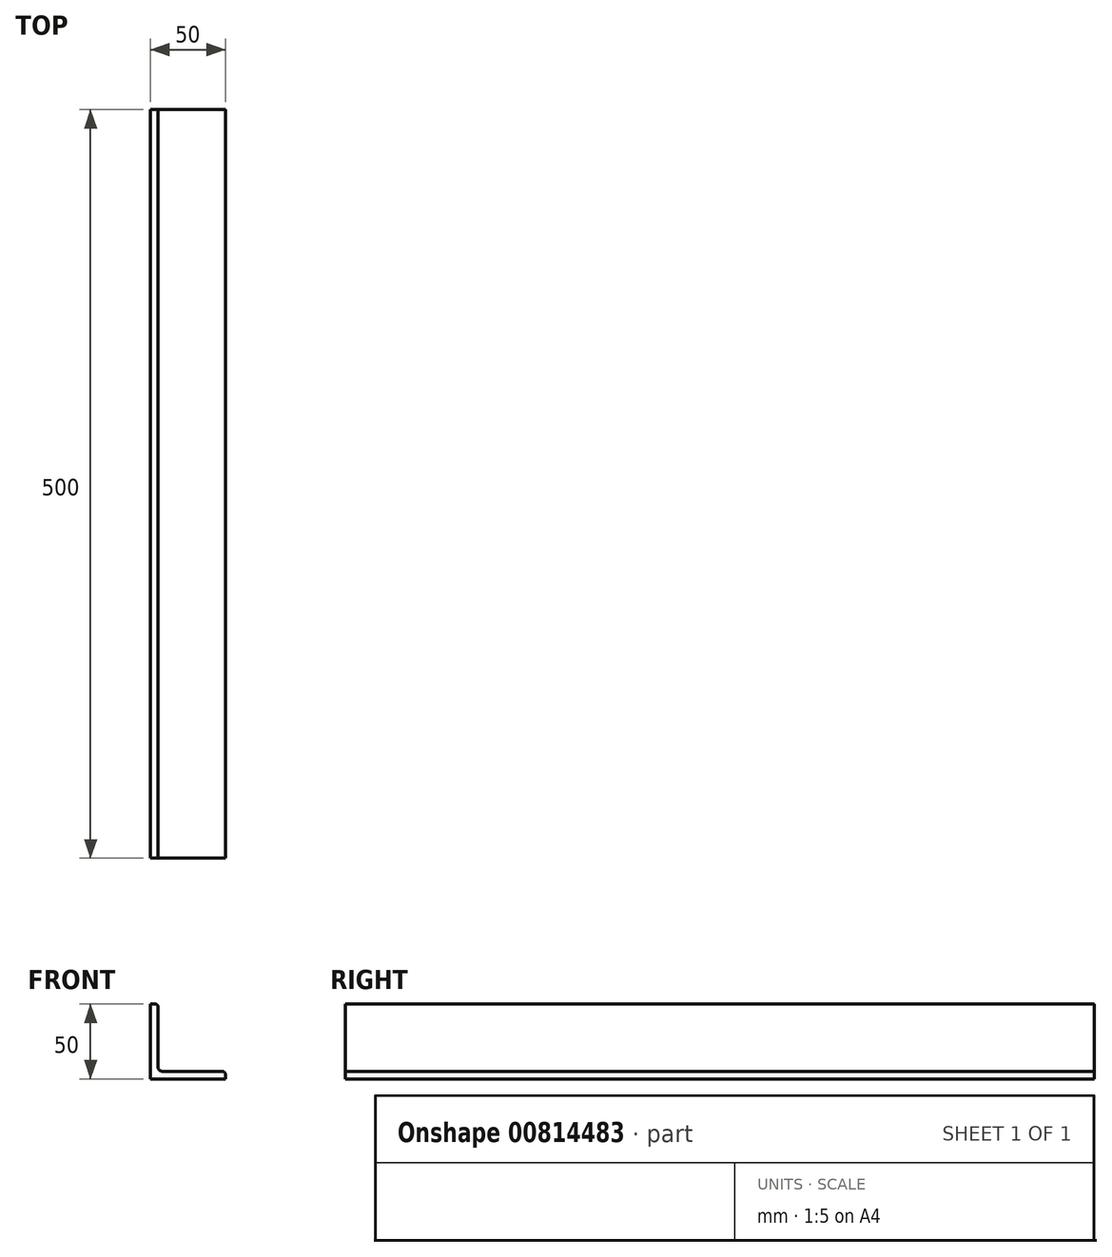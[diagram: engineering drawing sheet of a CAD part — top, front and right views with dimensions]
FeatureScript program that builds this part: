
annotation { "Feature Type Name" : "Feature", "Feature Type Description" : "" }
export const myFeature = defineFeature(function(context is Context, id is Id, definition is map)
    precondition{}
    {
        {
            var Q0;
            Q0=qCreatedBy(makeId("Front.planeOp"),FACE);
            var sketch = newSketch(context, id + "F0", { "sketchPlane" : qUnion([Q0])});
            skLineSegment(sketch, "E0", {"start": v(0, 0) * mm, "end": v(50, 0) * mm});
            skLineSegment(sketch, "E1", {"start": v(50, 0) * mm, "end": v(50, 3) * mm});
            skLineSegment(sketch, "E2", {"start": v(48, 5) * mm, "end": v(8, 5) * mm});
            skLineSegment(sketch, "E3", {"start": v(5, 8) * mm, "end": v(5, 48) * mm});
            skLineSegment(sketch, "E4", {"start": v(3, 50) * mm, "end": v(0, 50) * mm});
            skLineSegment(sketch, "E5", {"start": v(0, 50) * mm, "end": v(0, 0) * mm});
            skPoint(sketch, "E6.visualSharp", {"position": v(5, 50) * mm});
            skArc(sketch, "E6.filletArc", {"start": v(5, 48) * mm, "mid": v(4.41, 49.41) * mm, "end": v(3, 50) * mm});
            skPoint(sketch, "E7.visualSharp", {"position": v(50, 5) * mm});
            skArc(sketch, "E7.filletArc", {"start": v(50, 3) * mm, "mid": v(49.41, 4.41) * mm, "end": v(48, 5) * mm});
            skPoint(sketch, "E8.visualSharp", {"position": v(5, 5) * mm});
            skArc(sketch, "E8.filletArc", {"start": v(5, 8) * mm, "mid": v(5.88, 5.88) * mm, "end": v(8, 5) * mm});
            skSolve(sketch);
        }
        {
            assignVariable(context, id + "F1", {"name" : "Lenght", "anyValue" : 500});
        }
        {
            var Q0;
            Q0=makeQuery(id+"F0.imprint","IMPRINT",FACE,{"disambiguationData":[TD([[makeQuery(id+"F0.imprint","IMPRINT",EDGE,{"derivedFrom":sQuery(id+"F0.wireOp",EDGE,"E0")}),1.0]])]});
            extrude(context, id + "F2", {"entities" : qUnion([Q0]), "oppositeDirection" : true, "depth" : (getVariable(context, 'Lenght')) * mm, "offsetDistance" : 25 * mm});
        }
    });
